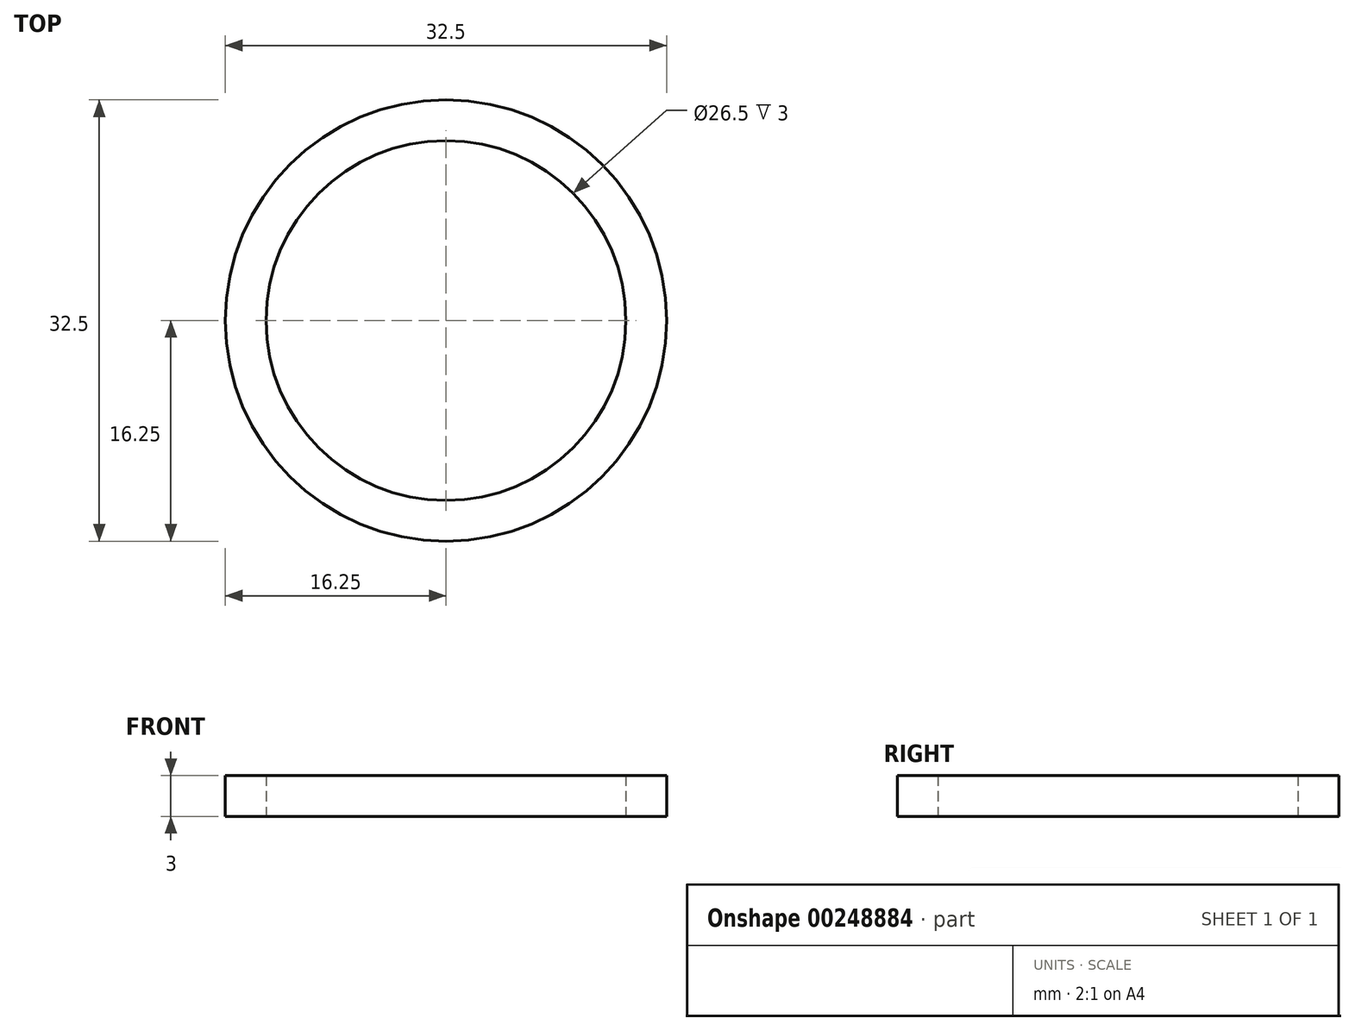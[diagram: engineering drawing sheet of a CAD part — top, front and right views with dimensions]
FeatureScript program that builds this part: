
annotation { "Feature Type Name" : "Feature", "Feature Type Description" : "" }
export const myFeature = defineFeature(function(context is Context, id is Id, definition is map)
    precondition{}
    {
        {
            var Q0;
            Q0=qCreatedBy(makeId("Top.planeOp"),FACE);
            var sketch = newSketch(context, id + "F0", { "sketchPlane" : qUnion([Q0])});
            skCircle(sketch, "E0", {"center": v(0, 0) * mm, "radius": 16.25 * mm});
            skCircle(sketch, "E1", {"center": v(0, 0) * mm, "radius": 13.25 * mm});
            skSolve(sketch);
        }
        {
            var Q0;
            Q0 = qSketchRegion(id + "F0", true);
            extrude(context, id + "F1", {"entities" : qUnion([Q0]), "depth" : 3 * mm, "offsetDistance" : 25 * mm});
        }
    });
